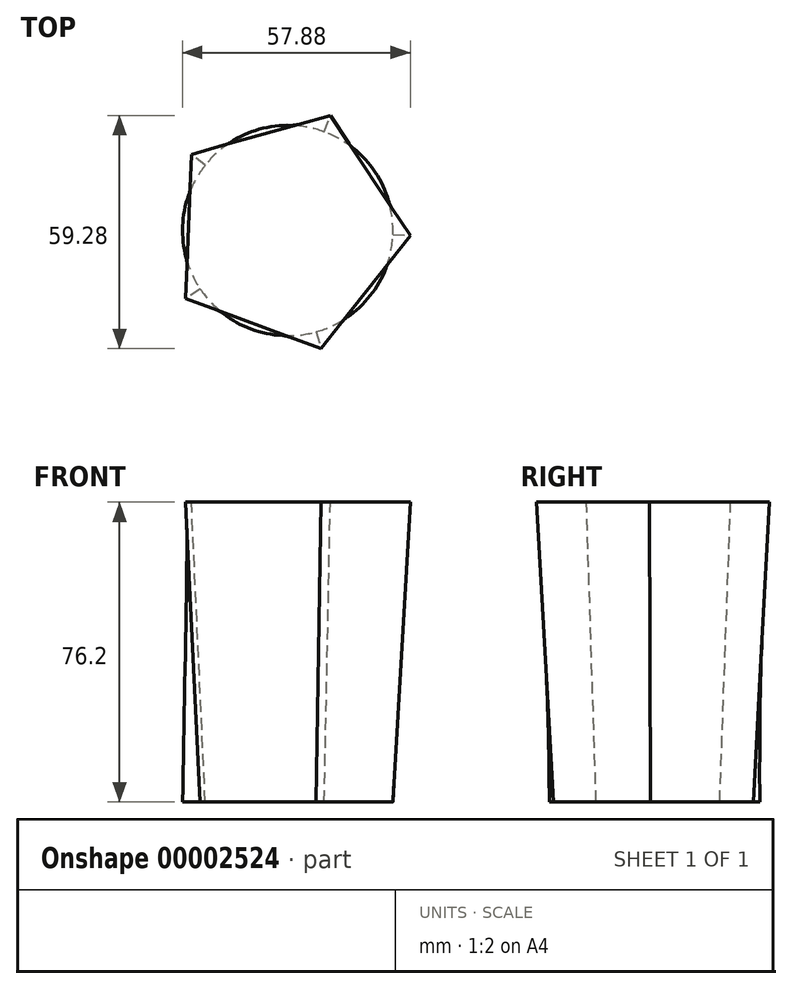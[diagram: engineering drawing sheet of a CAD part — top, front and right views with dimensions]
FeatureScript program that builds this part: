
annotation { "Feature Type Name" : "Feature", "Feature Type Description" : "" }
export const myFeature = defineFeature(function(context is Context, id is Id, definition is map)
    precondition{}
    {
        {
            var Q0;
            Q0=qCreatedBy(makeId("Top.planeOp"),FACE);
            var sketch = newSketch(context, id + "F0", { "sketchPlane" : qUnion([Q0])});
            skCircle(sketch, "E0", {"center": v(0, 0) * mm, "radius": 26.72 * mm});
            skSolve(sketch);
        }
        {
            var Q0;
            Q0=qCreatedBy(makeId("Top.planeOp"),FACE);
            cPlane(context, id + "F1", {"entities" : qUnion([Q0]), "cplaneType" : CPlaneType.OFFSET, "offset" : 76.2 * mm, "width" : 152.4 * mm, "height" : 152.4 * mm});
        }
        {
            var Q0;
            Q0=qCreatedBy(id+"F1.planeOp",FACE);
            var sketch = newSketch(context, id + "F2", { "sketchPlane" : qUnion([Q0])});
            skCircle(sketch, "E1.cCircle", {"center": v(0, 0) * mm, "radius": 25.23 * mm, "construction": true});
            skLineSegment(sketch, "E1.0", {"start": v(31.16, -1.26) * mm, "end": v(8.43, -30.03) * mm});
            skLineSegment(sketch, "E1.1", {"start": v(8.43, -30.03) * mm, "end": v(-25.95, -17.3) * mm});
            skLineSegment(sketch, "E1.2", {"start": v(-25.95, -17.3) * mm, "end": v(-24.47, 19.34) * mm});
            skLineSegment(sketch, "E1.3", {"start": v(-24.47, 19.34) * mm, "end": v(10.83, 29.25) * mm});
            skLineSegment(sketch, "E1.4", {"start": v(10.83, 29.25) * mm, "end": v(31.16, -1.26) * mm});
            skPoint(sketch, "E1.0.midPoint", {"position": v(19.8, -15.64) * mm});
            skSolve(sketch);
        }
        {
            var Q0;
            Q0=makeQuery(id+"F0.imprint","IMPRINT",FACE,{"disambiguationData":[TD([[makeQuery(id+"F0.imprint","IMPRINT",EDGE,{"derivedFrom":sQuery(id+"F0.wireOp",EDGE,"E0")}),1.0]])]});
            var Q1;
            Q1=makeQuery(id+"F2.imprint","IMPRINT",FACE,{"disambiguationData":[TD([[makeQuery(id+"F2.imprint","IMPRINT",EDGE,{"derivedFrom":sQuery(id+"F2.wireOp",EDGE,"E1.0")}),-1.0]])]});
            loft(context, id + "F3", {"sheetProfilesArray" : [{ "sheetProfileEntities" : qUnion([Q0]) }, { "sheetProfileEntities" : qUnion([Q1]) }]});
        }
    });
